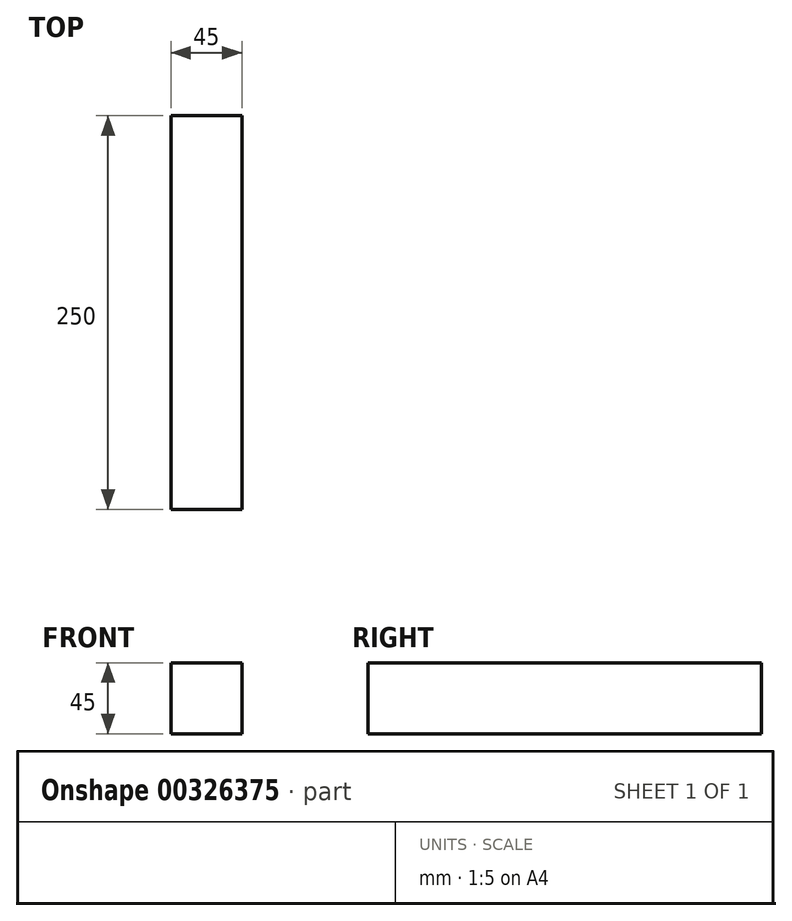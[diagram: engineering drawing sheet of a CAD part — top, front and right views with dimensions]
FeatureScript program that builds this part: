
annotation { "Feature Type Name" : "Feature", "Feature Type Description" : "" }
export const myFeature = defineFeature(function(context is Context, id is Id, definition is map)
    precondition{}
    {
        {
            var Q0;
            Q0=qCreatedBy(makeId("Front.planeOp"),FACE);
            var sketch = newSketch(context, id + "F0", { "sketchPlane" : qUnion([Q0])});
            skLineSegment(sketch, "E0.bottom", {"start": v(0, 0) * mm, "end": v(-45, 0) * mm});
            skLineSegment(sketch, "E0.top", {"start": v(0, 45) * mm, "end": v(-45, 45) * mm});
            skLineSegment(sketch, "E0.left", {"start": v(0, 0) * mm, "end": v(0, 45) * mm});
            skLineSegment(sketch, "E0.right", {"start": v(-45, 0) * mm, "end": v(-45, 45) * mm});
            skSolve(sketch);
        }
        {
            var Q0;
            Q0 = qSketchRegion(id + "F0", true);
            extrude(context, id + "F1", {"entities" : qUnion([Q0]), "depth" : 250 * mm});
        }
    });
